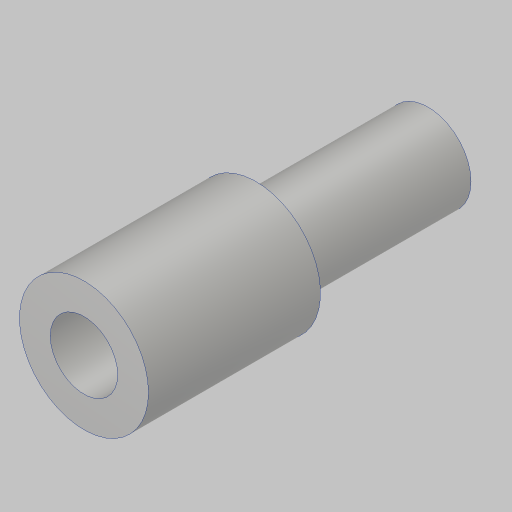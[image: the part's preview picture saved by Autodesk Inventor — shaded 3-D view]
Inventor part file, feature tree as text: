
AUTODESK INVENTOR PART (.ipt)
format: ipt  version: 2023.5 (Build 275446000, 446)  size: 249,344 bytes
history: native  units: in
note: dims shown in document units (in); Inventor stores cm internally (conversion verified against a paired STEP export)
features: sketch x3, extrude x2, hole x1, projected_geometry x1
ambient origin geometry x8: Origin, YZ Plane, XZ Plane, XY Plane, X Axis, Y Axis, Z Axis, Center Point
bodies: Solid1 (feature_tree)
feature tree (7):
  extrude  "Extrusion1"  Depth=1.0in TaperAngle=0.0deg
  hole  "Hole1"  [1 undecoded]
  extrude  "Extrusion2"  [1 undecoded]
  sketch  "Sketch1"  dims[d0=0.375in d1=1.0in d2=0.0in]
  sketch  "Sketch3"  dims[d3=0.196in d4=0.38in d5=0.385in d6=0.25in d7=0.5635in d8=0.536in d9=0.8108in d10=0.25in]
  sketch  "Sketch4"  dims[d11=0.5in d12=0.0in]
  projected_geometry  "Projected Loop1"
note: 2 required parameter values undecoded (feature->parameter linkage not recoverable at this tier; creation-order binding heuristic only, values carry confidence <= 0.55)
